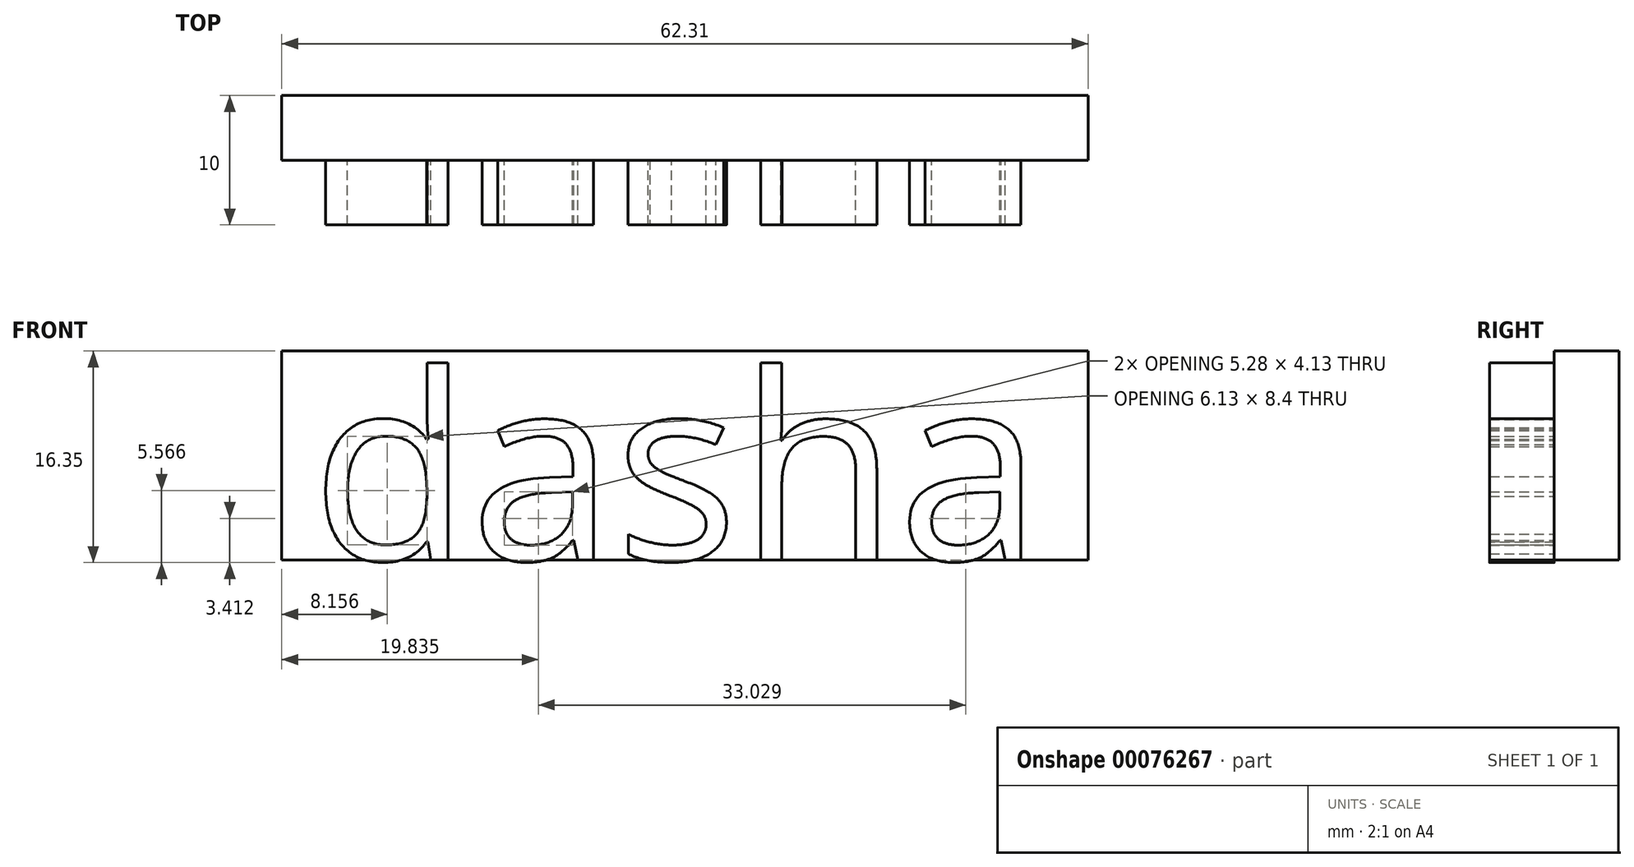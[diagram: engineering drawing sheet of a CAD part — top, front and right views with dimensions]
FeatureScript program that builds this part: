
annotation { "Feature Type Name" : "Feature", "Feature Type Description" : "" }
export const myFeature = defineFeature(function(context is Context, id is Id, definition is map)
    precondition{}
    {
        {
            var Q0;
            Q0=qCreatedBy(makeId("Front.planeOp"),FACE);
            var sketch = newSketch(context, id + "F0", { "sketchPlane" : qUnion([Q0])});
            skText(sketch, "E0", { "text": "dasha", "fontName": "OpenSans-Regular.ttf"});
            const initialGuessF0  = {"E0": [-0.02573, 0, 1, 0, 0.01444]};
            skSetInitialGuess(sketch, initialGuessF0);
            skSolve(sketch);
        }
        {
            var Q0;
            Q0 = qSketchRegion(id + "F0", true);
            extrude(context, id + "F1", {"entities" : qUnion([Q0]), "depth" : 5 * mm});
        }
        {
            var Q0;
            Q0=qCreatedBy(makeId("Front.planeOp"),FACE);
            var sketch = newSketch(context, id + "F2", { "sketchPlane" : qUnion([Q0])});
            skLineSegment(sketch, "E1.bottom", {"start": v(-28.01, 0) * mm, "end": v(34.3, 0) * mm});
            skLineSegment(sketch, "E1.top", {"start": v(-28.01, 16.15) * mm, "end": v(34.3, 16.15) * mm});
            skLineSegment(sketch, "E1.left", {"start": v(-28.01, 0) * mm, "end": v(-28.01, 16.15) * mm});
            skLineSegment(sketch, "E1.right", {"start": v(34.3, 0) * mm, "end": v(34.3, 16.15) * mm});
            skSolve(sketch);
        }
        {
            var Q0;
            Q0=makeQuery(id+"F2.imprint","IMPRINT",FACE,{"disambiguationData":[TD([[makeQuery(id+"F2.imprint","IMPRINT",EDGE,{"derivedFrom":sQuery(id+"F2.wireOp",EDGE,"E1.bottom")}),1.0]])]});
            extrude(context, id + "F3", {"entities" : qUnion([Q0]), "oppositeDirection" : true, "depth" : 5 * mm});
        }
    });
